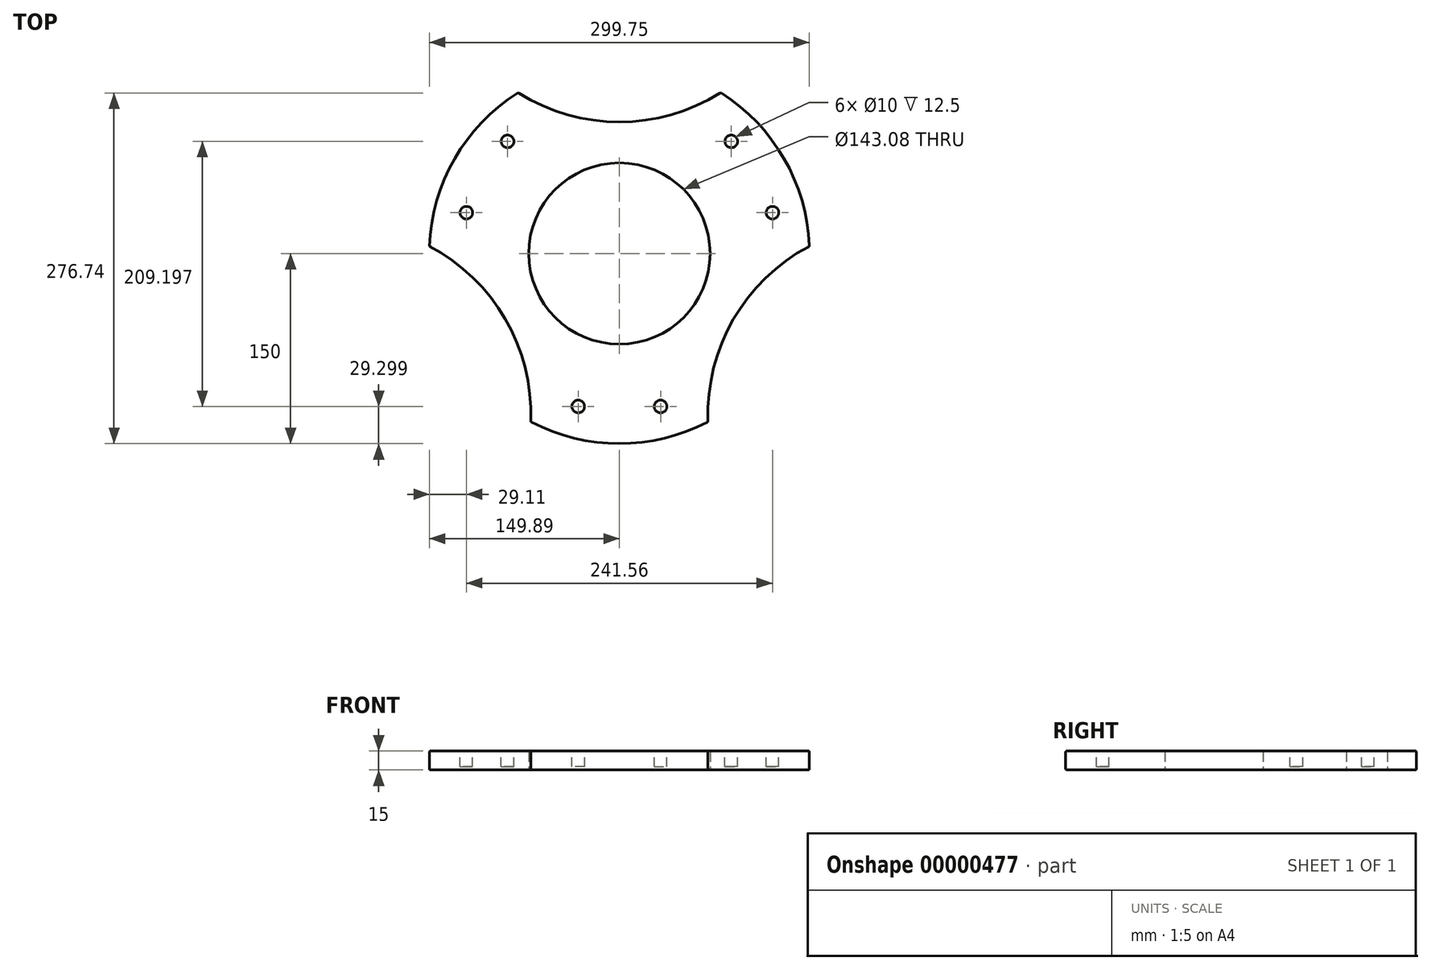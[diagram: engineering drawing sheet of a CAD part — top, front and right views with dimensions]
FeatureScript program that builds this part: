
annotation { "Feature Type Name" : "Feature", "Feature Type Description" : "" }
export const myFeature = defineFeature(function(context is Context, id is Id, definition is map)
    precondition{}
    {
        {
            var Q0;
            Q0     = qCreatedBy(makeId("Top.planeOp"), FACE);
            var sketch = newSketch(context, id + "F0", { "sketchPlane" : qUnion([Q0])});
            skLineSegment(sketch, "E0", {"start": v(0, 0) * mm, "end": v(0, -150) * mm, "construction": true});
            skArc(sketch, "E1", {"start": v(-61.95, 35.77) * mm, "mid": v(-61.95, -35.77) * mm, "end": v(0, -71.54) * mm});
            skArc(sketch, "E2", {"start": v(-129.9, 75) * mm, "mid": v(-144.12, 41.6) * mm, "end": v(-149.89, 5.76) * mm});
            skLineSegment(sketch, "E3", {"start": v(0, 0) * mm, "end": v(-129.9, -75) * mm, "construction": true});
            skArc(sketch, "E4", {"start": v(-69.95, -132.69) * mm, "mid": v(-89.94, -51.93) * mm, "end": v(-149.89, 5.76) * mm});
            skLineSegment(sketch, "E5", {"start": v(0, 0) * mm, "end": v(-129.9, 75) * mm, "construction": true});
            skLineSegment(sketch, "E6", {"start": v(-129.9, 75) * mm, "end": v(-61.95, 35.77) * mm});
            skLineSegment(sketch, "E7", {"start": v(0, -71.54) * mm, "end": v(0, -150) * mm});
            skArc(sketch, "E8.trimOffspring", {"start": v(-69.95, -132.69) * mm, "mid": v(-36.03, -145.6) * mm, "end": v(0, -150) * mm});
            skSolve(sketch);
        }
        {
            var Q0;
            Q0=makeQuery(id+"F0.imprint","IMPRINT",FACE,{"disambiguationData":[TD([[makeQuery(id+"F0.imprint","IMPRINT",EDGE,{"derivedFrom":sQuery(id+"F0.wireOp",EDGE,"E1")}),-1.0]])]});
            extrude(context, id + "F1", {"entities" : qUnion([Q0]), "depth" : 15 * mm});
        }
        {
            var Q0;
            Q0=makeQuery(id+"F1.opExtrude","CAP_FACE",FACE,{"disambiguationData":[OSD([sQuery(id+"F0.wireOp",EDGE,"E1"),sQuery(id+"F0.wireOp",EDGE,"E2"),sQuery(id+"F0.wireOp",EDGE,"E4"),sQuery(id+"F0.wireOp",EDGE,"E6"),sQuery(id+"F0.wireOp",EDGE,"E7"),sQuery(id+"F0.wireOp",EDGE,"E8.trimOffspring")])],"isStart":false});
            var sketch = newSketch(context, id + "F2", { "sketchPlane" : qUnion([Q0])});
            skCircle(sketch, "E9", {"center": v(-32.5, -120.7) * mm, "radius": 5 * mm});
            skCircle(sketch, "E10", {"center": v(0, 0) * mm, "radius": 125 * mm, "construction": true});
            skLineSegment(sketch, "E11.0", {"start": v(0, 0) * mm, "end": v(-129.9, -75) * mm, "construction": true});
            skLineSegment(sketch, "E12.0", {"start": v(0, 0) * mm, "end": v(0, -150) * mm, "construction": true});
            skSolve(sketch);
        }
        {
            var Q0;
            Q0=makeQuery(id+"F2.imprint","IMPRINT",FACE,{"disambiguationData":[TD([[makeQuery(id+"F2.imprint","IMPRINT",EDGE,{"derivedFrom":sQuery(id+"F2.wireOp",EDGE,"E9")}),1.0]])]});
            extrude(context, id + "F3", {"entities" : qUnion([Q0]), "oppositeDirection" : true, "depth" : 12.5 * mm});
        }
        {
            var Q0;
            Q0=sQuery(id+"F0.wireOp",EDGE,"E3");
            cPlane(context, id + "F4", {"entities" : qUnion([Q0]), "cplaneType" : CPlaneType.LINE_ANGLE, "offset" : 150 * mm, "angle" : 0 * degree, "width" : 150 * mm, "height" : 150 * mm});
        }
        {
            var Q0;
            Q0=makeQuery(id+"F3.opExtrude","SWEPT_BODY",BODY,{"disambiguationData":[OSD([sQuery(id+"F2.wireOp",EDGE,"E9")])]});
            var Q1;
            Q1=qCreatedBy(id+"F4.planeOp",FACE);
            mirror(context, id + "F5", {"entities" : qUnion([Q0]), "mirrorPlane" : qUnion([Q1])});
        }
        {
            var Q0;
            Q0=makeQuery(id+"F3.opExtrude","SWEPT_BODY",BODY,{"disambiguationData":[OSD([sQuery(id+"F2.wireOp",EDGE,"E9")])]});
            var Q1;
            Q1=makeQuery(id+"F5.opPattern","COPY",BODY,{"derivedFrom":makeQuery(id+"F3.opExtrude","SWEPT_BODY",BODY,{"disambiguationData":[OSD([sQuery(id+"F2.wireOp",EDGE,"E9")])]}),"instanceName":"1"});
            var Q2;
            Q2=makeQuery(id+"F1.opExtrude","SWEPT_BODY",BODY,{"disambiguationData":[OSD([sQuery(id+"F0.wireOp",EDGE,"E1"),sQuery(id+"F0.wireOp",EDGE,"E2"),sQuery(id+"F0.wireOp",EDGE,"E4"),sQuery(id+"F0.wireOp",EDGE,"E6"),sQuery(id+"F0.wireOp",EDGE,"E7"),sQuery(id+"F0.wireOp",EDGE,"E8.trimOffspring")])]});
            booleanBodies(context, id + "F6", {"operationType" : BooleanOperationType.SUBTRACTION, "tools" : qUnion([Q0, Q1]), "targets" : qUnion([Q2])});
        }
        {
            var Q0;
            Q0=makeQuery(id+"F1.opExtrude","SWEPT_BODY",BODY,{"disambiguationData":[OSD([sQuery(id+"F0.wireOp",EDGE,"E1"),sQuery(id+"F0.wireOp",EDGE,"E2"),sQuery(id+"F0.wireOp",EDGE,"E4"),sQuery(id+"F0.wireOp",EDGE,"E6"),sQuery(id+"F0.wireOp",EDGE,"E7"),sQuery(id+"F0.wireOp",EDGE,"E8.trimOffspring")])]});
            var Q1;
            Q1=makeQuery(id+"F1.opExtrude","SWEPT_FACE",FACE,{"disambiguationData":[OSD([sQuery(id+"F0.wireOp",EDGE,"E1")])]});
            circularPattern(context, id + "F7", {"entities" : qUnion([Q0]), "axis" : qUnion([Q1]), "angle" : 360 * degree, "instanceCount" : 3, "equalSpace" : true});
        }
        {
            var Q0;
            Q0=makeQuery(id+"F1.opExtrude","SWEPT_BODY",BODY,{"disambiguationData":[OSD([sQuery(id+"F0.wireOp",EDGE,"E1"),sQuery(id+"F0.wireOp",EDGE,"E2"),sQuery(id+"F0.wireOp",EDGE,"E4"),sQuery(id+"F0.wireOp",EDGE,"E6"),sQuery(id+"F0.wireOp",EDGE,"E7"),sQuery(id+"F0.wireOp",EDGE,"E8.trimOffspring")])]});
            var Q1;
            Q1=makeQuery(id+"F7.opPattern","COPY",BODY,{"derivedFrom":makeQuery(id+"F1.opExtrude","SWEPT_BODY",BODY,{"disambiguationData":[OSD([sQuery(id+"F0.wireOp",EDGE,"E1"),sQuery(id+"F0.wireOp",EDGE,"E2"),sQuery(id+"F0.wireOp",EDGE,"E4"),sQuery(id+"F0.wireOp",EDGE,"E6"),sQuery(id+"F0.wireOp",EDGE,"E7"),sQuery(id+"F0.wireOp",EDGE,"E8.trimOffspring")])]}),"instanceName":"2"});
            var Q2;
            Q2=makeQuery(id+"F7.opPattern","COPY",BODY,{"derivedFrom":makeQuery(id+"F1.opExtrude","SWEPT_BODY",BODY,{"disambiguationData":[OSD([sQuery(id+"F0.wireOp",EDGE,"E1"),sQuery(id+"F0.wireOp",EDGE,"E2"),sQuery(id+"F0.wireOp",EDGE,"E4"),sQuery(id+"F0.wireOp",EDGE,"E6"),sQuery(id+"F0.wireOp",EDGE,"E7"),sQuery(id+"F0.wireOp",EDGE,"E8.trimOffspring")])]}),"instanceName":"1"});
            booleanBodies(context, id + "F8", {"operationType" : BooleanOperationType.UNION, "tools" : qUnion([Q0, Q1, Q2])});
        }
        {
            var Q0;
            Q0=makeQuery(id+"F8.opBoolean","MERGE",EDGE,{"derivedFrom":[makeQuery(id+"F1.opExtrude","CAP_EDGE",EDGE,{"disambiguationData":[OSD([sQuery(id+"F0.wireOp",EDGE,"E8.trimOffspring")])],"isStart":false}),makeQuery(id+"F7.opPattern","COPY",EDGE,{"derivedFrom":makeQuery(id+"F1.opExtrude","CAP_EDGE",EDGE,{"disambiguationData":[OSD([sQuery(id+"F0.wireOp",EDGE,"E2")])],"isStart":false}),"instanceName":"1"})]});
            var Q1;
            Q1=makeQuery(id+"F7.opPattern","COPY",EDGE,{"derivedFrom":makeQuery(id+"F1.opExtrude","SWEPT_EDGE",EDGE,{"disambiguationData":[OSD([sQuery(id+"F0.wireOp",EDGE,"E2"),sQuery(id+"F0.wireOp",EDGE,"E4")])]}),"instanceName":"1"});
            var Q2;
            Q2=makeQuery(id+"F7.opPattern","COPY",EDGE,{"derivedFrom":makeQuery(id+"F1.opExtrude","CAP_EDGE",EDGE,{"disambiguationData":[OSD([sQuery(id+"F0.wireOp",EDGE,"E4")])],"isStart":false}),"instanceName":"1"});
            var Q3;
            Q3=makeQuery(id+"F7.opPattern","COPY",EDGE,{"derivedFrom":makeQuery(id+"F1.opExtrude","SWEPT_EDGE",EDGE,{"disambiguationData":[OSD([sQuery(id+"F0.wireOp",EDGE,"E4"),sQuery(id+"F0.wireOp",EDGE,"E8.trimOffspring")])]}),"instanceName":"1"});
            var Q4;
            Q4=makeQuery(id+"F8.opBoolean","MERGE",EDGE,{"derivedFrom":[makeQuery(id+"F7.opPattern","COPY",EDGE,{"derivedFrom":makeQuery(id+"F1.opExtrude","CAP_EDGE",EDGE,{"disambiguationData":[OSD([sQuery(id+"F0.wireOp",EDGE,"E8.trimOffspring")])],"isStart":false}),"instanceName":"1"}),makeQuery(id+"F7.opPattern","COPY",EDGE,{"derivedFrom":makeQuery(id+"F1.opExtrude","CAP_EDGE",EDGE,{"disambiguationData":[OSD([sQuery(id+"F0.wireOp",EDGE,"E2")])],"isStart":false}),"instanceName":"2"})]});
            var Q5;
            Q5=makeQuery(id+"F7.opPattern","COPY",EDGE,{"derivedFrom":makeQuery(id+"F1.opExtrude","SWEPT_EDGE",EDGE,{"disambiguationData":[OSD([sQuery(id+"F0.wireOp",EDGE,"E2"),sQuery(id+"F0.wireOp",EDGE,"E4")])]}),"instanceName":"2"});
            var Q6;
            Q6=makeQuery(id+"F7.opPattern","COPY",EDGE,{"derivedFrom":makeQuery(id+"F1.opExtrude","CAP_EDGE",EDGE,{"disambiguationData":[OSD([sQuery(id+"F0.wireOp",EDGE,"E4")])],"isStart":false}),"instanceName":"2"});
            var Q7;
            Q7=makeQuery(id+"F7.opPattern","COPY",EDGE,{"derivedFrom":makeQuery(id+"F1.opExtrude","SWEPT_EDGE",EDGE,{"disambiguationData":[OSD([sQuery(id+"F0.wireOp",EDGE,"E4"),sQuery(id+"F0.wireOp",EDGE,"E8.trimOffspring")])]}),"instanceName":"2"});
            var Q8;
            Q8=makeQuery(id+"F8.opBoolean","MERGE",EDGE,{"derivedFrom":[makeQuery(id+"F1.opExtrude","CAP_EDGE",EDGE,{"disambiguationData":[OSD([sQuery(id+"F0.wireOp",EDGE,"E2")])],"isStart":false}),makeQuery(id+"F7.opPattern","COPY",EDGE,{"derivedFrom":makeQuery(id+"F1.opExtrude","CAP_EDGE",EDGE,{"disambiguationData":[OSD([sQuery(id+"F0.wireOp",EDGE,"E8.trimOffspring")])],"isStart":false}),"instanceName":"2"})]});
            var Q9;
            Q9=makeQuery(id+"F1.opExtrude","CAP_EDGE",EDGE,{"disambiguationData":[OSD([sQuery(id+"F0.wireOp",EDGE,"E4")])],"isStart":false});
            var Q10;
            Q10=makeQuery(id+"F1.opExtrude","SWEPT_EDGE",EDGE,{"disambiguationData":[OSD([sQuery(id+"F0.wireOp",EDGE,"E4"),sQuery(id+"F0.wireOp",EDGE,"E8.trimOffspring")])]});
            var Q11;
            Q11=makeQuery(id+"F8.opBoolean","MERGE",EDGE,{"derivedFrom":[makeQuery(id+"F1.opExtrude","CAP_EDGE",EDGE,{"disambiguationData":[OSD([sQuery(id+"F0.wireOp",EDGE,"E8.trimOffspring")])],"isStart":true}),makeQuery(id+"F7.opPattern","COPY",EDGE,{"derivedFrom":makeQuery(id+"F1.opExtrude","CAP_EDGE",EDGE,{"disambiguationData":[OSD([sQuery(id+"F0.wireOp",EDGE,"E2")])],"isStart":true}),"instanceName":"1"})]});
            var Q12;
            Q12=makeQuery(id+"F1.opExtrude","CAP_EDGE",EDGE,{"disambiguationData":[OSD([sQuery(id+"F0.wireOp",EDGE,"E4")])],"isStart":true});
            var Q13;
            Q13=makeQuery(id+"F7.opPattern","COPY",EDGE,{"derivedFrom":makeQuery(id+"F1.opExtrude","CAP_EDGE",EDGE,{"disambiguationData":[OSD([sQuery(id+"F0.wireOp",EDGE,"E4")])],"isStart":true}),"instanceName":"1"});
            var Q14;
            Q14=makeQuery(id+"F8.opBoolean","MERGE",EDGE,{"derivedFrom":[makeQuery(id+"F7.opPattern","COPY",EDGE,{"derivedFrom":makeQuery(id+"F1.opExtrude","CAP_EDGE",EDGE,{"disambiguationData":[OSD([sQuery(id+"F0.wireOp",EDGE,"E8.trimOffspring")])],"isStart":true}),"instanceName":"1"}),makeQuery(id+"F7.opPattern","COPY",EDGE,{"derivedFrom":makeQuery(id+"F1.opExtrude","CAP_EDGE",EDGE,{"disambiguationData":[OSD([sQuery(id+"F0.wireOp",EDGE,"E2")])],"isStart":true}),"instanceName":"2"})]});
            var Q15;
            Q15=makeQuery(id+"F7.opPattern","COPY",EDGE,{"derivedFrom":makeQuery(id+"F1.opExtrude","CAP_EDGE",EDGE,{"disambiguationData":[OSD([sQuery(id+"F0.wireOp",EDGE,"E4")])],"isStart":true}),"instanceName":"2"});
            var Q16;
            Q16=makeQuery(id+"F8.opBoolean","MERGE",EDGE,{"derivedFrom":[makeQuery(id+"F1.opExtrude","CAP_EDGE",EDGE,{"disambiguationData":[OSD([sQuery(id+"F0.wireOp",EDGE,"E2")])],"isStart":true}),makeQuery(id+"F7.opPattern","COPY",EDGE,{"derivedFrom":makeQuery(id+"F1.opExtrude","CAP_EDGE",EDGE,{"disambiguationData":[OSD([sQuery(id+"F0.wireOp",EDGE,"E8.trimOffspring")])],"isStart":true}),"instanceName":"2"})]});
            var Q17;
            {var subQ0=makeQuery(id+"F1.opExtrude","CAP_EDGE",EDGE,{"disambiguationData":[OSD([sQuery(id+"F0.wireOp",EDGE,"E1")])],"isStart":true});Q17=makeQuery(id+"F8.opBoolean","MERGE",EDGE,{"derivedFrom":[subQ0,makeQuery(id+"F7.opPattern","COPY",EDGE,{"derivedFrom":subQ0,"instanceName":"1"}),makeQuery(id+"F7.opPattern","COPY",EDGE,{"derivedFrom":subQ0,"instanceName":"2"})]});}
            var Q18;
            {var subQ0=makeQuery(id+"F1.opExtrude","CAP_EDGE",EDGE,{"disambiguationData":[OSD([sQuery(id+"F0.wireOp",EDGE,"E1")])],"isStart":false});Q18=makeQuery(id+"F8.opBoolean","MERGE",EDGE,{"derivedFrom":[subQ0,makeQuery(id+"F7.opPattern","COPY",EDGE,{"derivedFrom":subQ0,"instanceName":"1"}),makeQuery(id+"F7.opPattern","COPY",EDGE,{"derivedFrom":subQ0,"instanceName":"2"})]});}
            fillet(context, id + "F9", {"entities" : qUnion([Q0, Q1, Q2, Q3, Q4, Q5, Q6, Q7, Q8, Q9, Q10, Q11, Q12, Q13, Q14, Q15, Q16, Q17, Q18]), "radius" : 1 * mm, "tangentPropagation" : true, "allowEdgeOverflow" : false});
        }
    });
